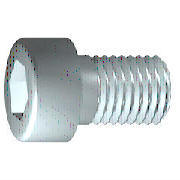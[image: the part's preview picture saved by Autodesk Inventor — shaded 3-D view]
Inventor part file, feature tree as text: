
AUTODESK INVENTOR PART (.ipt)
format: ipt  version: 2024.2 (Build 282272000, 272)  size: 214,016 bytes
history: native  units: mm (DEFAULTED — no unit token found)
features: extrude x2, plane x1, fillet x1, chamfer x1, projected_geometry x1
ambient origin geometry x7: Origin, YZ Plane, XY Plane, X Axis, Y Axis, Z Axis, Center Point
bodies: Solid1 (feature_tree), Body (feature_tree)
feature tree (6):
  extrude  "Slot"  Depth=3.75mm
  plane  "Work Plane1"
  fillet  "Fillet2"  Radius=0.306825mm
  extrude  "Extrusion3"  Depth=3.0mm
  chamfer  "Chamfer3"  Distance=1.3mm
  projected_geometry  "Projected Loop1"
